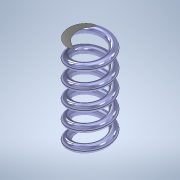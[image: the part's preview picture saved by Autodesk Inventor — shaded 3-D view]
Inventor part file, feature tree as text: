
AUTODESK INVENTOR PART (.ipt)
format: ipt  version: 2020 (Build 240168000, 168)  size: 331,264 bytes
history: native  units: mm
features: sketch x2, extrude x1, helix x1
ambient origin geometry x8: Origin, YZ Plane, XZ Plane, XY Plane, X Axis, Y Axis, Z Axis, Center Point
bodies: Solid1 (feature_tree)
feature tree (4):
  extrude  "Extrusion1"  Depth=150.0mm TaperAngle=0.0deg
  helix  "Coil1"  [1 undecoded]
  sketch  "Sketch1"  dims[d0=70.0mm d1=150.0mm d2=0.0mm d3=12.5mm]
  sketch  "Sketch2"  dims[d6=156.25mm d7=30.0mm d8=175.0mm d9=10.0mm d10=0.0mm d11=90.0deg d12=90.0deg d13=0.0mm d14=0.0mm d15=57.51mm]
note: 1 required parameter value undecoded (feature->parameter linkage not recoverable at this tier; creation-order binding heuristic only, values carry confidence <= 0.55)
